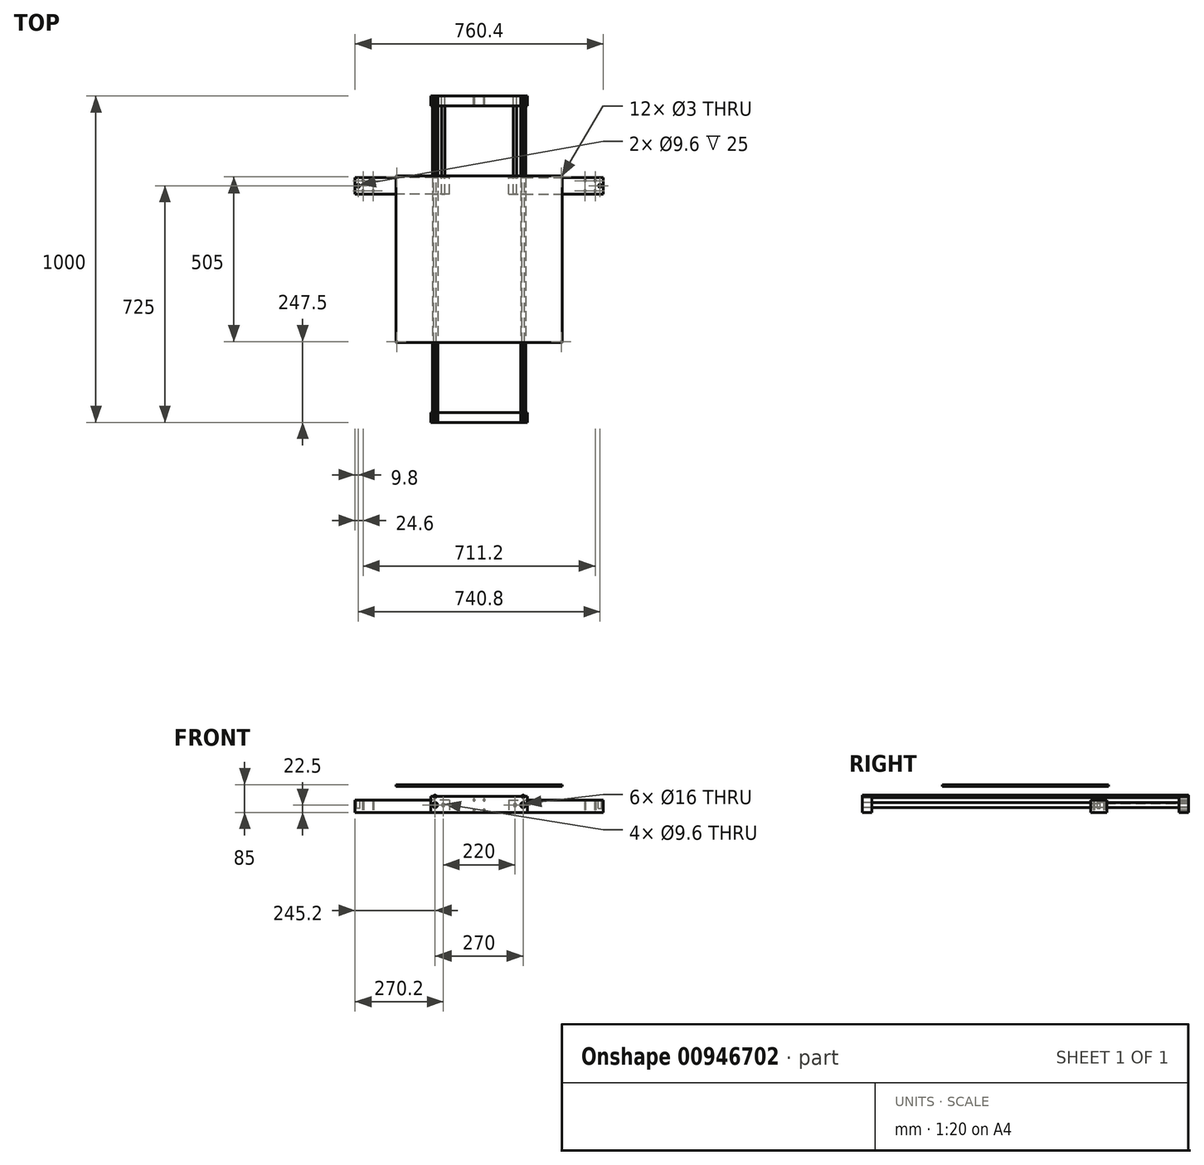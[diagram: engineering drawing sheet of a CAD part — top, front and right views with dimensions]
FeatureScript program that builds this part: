
annotation { "Feature Type Name" : "Feature", "Feature Type Description" : "" }
export const myFeature = defineFeature(function(context is Context, id is Id, definition is map)
    precondition{}
    {
        {
            var Q0;
            Q0=qCreatedBy(makeId("Top.planeOp"),FACE);
            var sketch = newSketch(context, id + "F0", { "sketchPlane" : qUnion([Q0])});
            skLineSegment(sketch, "E0.bottom", {"start": v(255, -255) * mm, "end": v(-255, -255) * mm});
            skLineSegment(sketch, "E0.top", {"start": v(255, 255) * mm, "end": v(-255, 255) * mm});
            skLineSegment(sketch, "E0.left", {"start": v(255, -255) * mm, "end": v(255, 255) * mm});
            skLineSegment(sketch, "E0.right", {"start": v(-255, -255) * mm, "end": v(-255, 255) * mm});
            skPoint(sketch, "E0.middle", {"position": v(0, 0) * mm});
            skLineSegment(sketch, "E1.bottom", {"start": v(-252.5, 252.5) * mm, "end": v(252.5, 252.5) * mm, "construction": true});
            skLineSegment(sketch, "E1.top", {"start": v(-252.5, -252.5) * mm, "end": v(252.5, -252.5) * mm, "construction": true});
            skLineSegment(sketch, "E1.left", {"start": v(-252.5, 252.5) * mm, "end": v(-252.5, -252.5) * mm, "construction": true});
            skLineSegment(sketch, "E1.right", {"start": v(252.5, 252.5) * mm, "end": v(252.5, -252.5) * mm, "construction": true});
            skCircle(sketch, "E2", {"center": v(-252.5, 252.5) * mm, "radius": 1.5 * mm});
            skCircle(sketch, "E3", {"center": v(252.5, 252.5) * mm, "radius": 1.5 * mm});
            skCircle(sketch, "E4", {"center": v(252.5, -252.5) * mm, "radius": 1.5 * mm});
            skCircle(sketch, "E5", {"center": v(-252.5, -252.5) * mm, "radius": 1.5 * mm});
            skSolve(sketch);
        }
        {
            var Q0;
            Q0=makeQuery(id+"F0.imprint","IMPRINT",FACE,{"disambiguationData":[TD([[makeQuery(id+"F0.imprint","IMPRINT",EDGE,{"derivedFrom":sQuery(id+"F0.wireOp",EDGE,"E0.bottom")}),-1.0]])]});
            extrude(context, id + "F1", {"entities" : qUnion([Q0]), "depth" : 5 * mm, "offsetDistance" : 25 * mm});
        }
        {
            var Q0;
            Q0=makeQuery(id+"F1.opExtrude","CAP_FACE",FACE,{"disambiguationData":[OSD([sQuery(id+"F0.wireOp",EDGE,"E0.bottom"),sQuery(id+"F0.wireOp",EDGE,"E0.top"),sQuery(id+"F0.wireOp",EDGE,"E0.left"),sQuery(id+"F0.wireOp",EDGE,"E0.right")])],"isStart":true});
            cPlane(context, id + "F2", {"entities" : qUnion([Q0]), "cplaneType" : CPlaneType.OFFSET, "offset" : 20 * mm, "width" : 150 * mm, "height" : 150 * mm});
        }
        {
            var Q0;
            Q0=qCreatedBy(id+"F2.planeOp",FACE);
            var sketch = newSketch(context, id + "F3", { "sketchPlane" : qUnion([Q0])});
            skCircle(sketch, "E6.0", {"center": v(-252.5, 252.5) * mm, "radius": 1.5 * mm});
            skCircle(sketch, "E6.1", {"center": v(252.5, 252.5) * mm, "radius": 1.5 * mm});
            skCircle(sketch, "E6.2", {"center": v(252.5, -252.5) * mm, "radius": 1.5 * mm});
            skCircle(sketch, "E6.3", {"center": v(-252.5, -252.5) * mm, "radius": 1.5 * mm});
            skLineSegment(sketch, "E7.bottom", {"start": v(135, -135) * mm, "end": v(-135, -135) * mm, "construction": true});
            skLineSegment(sketch, "E7.top", {"start": v(135, 135) * mm, "end": v(-135, 135) * mm, "construction": true});
            skLineSegment(sketch, "E7.left", {"start": v(135, -135) * mm, "end": v(135, 135) * mm, "construction": true});
            skLineSegment(sketch, "E7.right", {"start": v(-135, -135) * mm, "end": v(-135, 135) * mm, "construction": true});
            skPoint(sketch, "E7.middle", {"position": v(0, 0) * mm});
            skCircle(sketch, "E8", {"center": v(-252.5, 252.5) * mm, "radius": 2.5 * mm});
            skCircle(sketch, "E9", {"center": v(252.5, 252.5) * mm, "radius": 2.5 * mm});
            skCircle(sketch, "E10", {"center": v(252.5, -252.5) * mm, "radius": 2.5 * mm});
            skCircle(sketch, "E11", {"center": v(-252.5, -252.5) * mm, "radius": 2.5 * mm});
            skLineSegment(sketch, "E12", {"start": v(-254.27, 250.73) * mm, "end": v(-250.73, 254.27) * mm, "construction": true});
            skLineSegment(sketch, "E13", {"start": v(250.73, 254.27) * mm, "end": v(254.27, 250.73) * mm, "construction": true});
            skLineSegment(sketch, "E14", {"start": v(250.73, -254.27) * mm, "end": v(254.27, -250.73) * mm, "construction": true});
            skLineSegment(sketch, "E15", {"start": v(-254.27, -250.73) * mm, "end": v(-250.73, -254.27) * mm, "construction": true});
            skLineSegment(sketch, "E16", {"start": v(0, -135) * mm, "end": v(-250.73, -254.27) * mm});
            skLineSegment(sketch, "E17", {"start": v(0, -135) * mm, "end": v(250.73, -254.27) * mm});
            skLineSegment(sketch, "E18", {"start": v(-254.27, -250.73) * mm, "end": v(-135, 0) * mm});
            skLineSegment(sketch, "E19", {"start": v(-135, 0) * mm, "end": v(-254.27, 250.73) * mm});
            skLineSegment(sketch, "E20", {"start": v(-250.73, 254.27) * mm, "end": v(0, 135) * mm});
            skLineSegment(sketch, "E21", {"start": v(0, 135) * mm, "end": v(250.73, 254.27) * mm});
            skLineSegment(sketch, "E22", {"start": v(254.27, 250.73) * mm, "end": v(135, 0) * mm});
            skLineSegment(sketch, "E23", {"start": v(135, 0) * mm, "end": v(254.27, -250.73) * mm});
            skLineSegment(sketch, "E24.bottom", {"start": v(-135, 67.5) * mm, "end": v(135, 67.5) * mm, "construction": true});
            skLineSegment(sketch, "E24.top", {"start": v(-135, -67.5) * mm, "end": v(135, -67.5) * mm, "construction": true});
            skLineSegment(sketch, "E24.left", {"start": v(-135, 67.5) * mm, "end": v(-135, -67.5) * mm, "construction": true});
            skLineSegment(sketch, "E24.right", {"start": v(135, 67.5) * mm, "end": v(135, -67.5) * mm, "construction": true});
            skLineSegment(sketch, "E25.bottom", {"start": v(-123, -76.5) * mm, "end": v(-147, -76.5) * mm, "construction": true});
            skLineSegment(sketch, "E25.top", {"start": v(-123, -58.5) * mm, "end": v(-147, -58.5) * mm, "construction": true});
            skLineSegment(sketch, "E25.left", {"start": v(-123, -76.5) * mm, "end": v(-123, -58.5) * mm, "construction": true});
            skLineSegment(sketch, "E25.right", {"start": v(-147, -76.5) * mm, "end": v(-147, -58.5) * mm, "construction": true});
            skPoint(sketch, "E25.middle", {"position": v(-135, -67.5) * mm});
            skLineSegment(sketch, "E26.bottom", {"start": v(123, -76.5) * mm, "end": v(147, -76.5) * mm, "construction": true});
            skLineSegment(sketch, "E26.top", {"start": v(123, -58.5) * mm, "end": v(147, -58.5) * mm, "construction": true});
            skLineSegment(sketch, "E26.left", {"start": v(123, -76.5) * mm, "end": v(123, -58.5) * mm, "construction": true});
            skLineSegment(sketch, "E26.right", {"start": v(147, -76.5) * mm, "end": v(147, -58.5) * mm, "construction": true});
            skPoint(sketch, "E26.middle", {"position": v(135, -67.5) * mm});
            skLineSegment(sketch, "E27.bottom", {"start": v(123, 58.5) * mm, "end": v(147, 58.5) * mm, "construction": true});
            skLineSegment(sketch, "E27.top", {"start": v(123, 76.5) * mm, "end": v(147, 76.5) * mm, "construction": true});
            skLineSegment(sketch, "E27.left", {"start": v(123, 58.5) * mm, "end": v(123, 76.5) * mm, "construction": true});
            skLineSegment(sketch, "E27.right", {"start": v(147, 58.5) * mm, "end": v(147, 76.5) * mm, "construction": true});
            skPoint(sketch, "E27.middle", {"position": v(135, 67.5) * mm});
            skLineSegment(sketch, "E28.bottom", {"start": v(-123, 58.5) * mm, "end": v(-147, 58.5) * mm, "construction": true});
            skLineSegment(sketch, "E28.top", {"start": v(-123, 76.5) * mm, "end": v(-147, 76.5) * mm, "construction": true});
            skLineSegment(sketch, "E28.left", {"start": v(-123, 58.5) * mm, "end": v(-123, 76.5) * mm, "construction": true});
            skLineSegment(sketch, "E28.right", {"start": v(-147, 58.5) * mm, "end": v(-147, 76.5) * mm, "construction": true});
            skPoint(sketch, "E28.middle", {"position": v(-135, 67.5) * mm});
            skCircle(sketch, "E29", {"center": v(-147, -76.5) * mm, "radius": 2.05 * mm});
            skCircle(sketch, "E30", {"center": v(-147, -58.5) * mm, "radius": 2.05 * mm});
            skCircle(sketch, "E31", {"center": v(-123, -58.5) * mm, "radius": 2.05 * mm});
            skCircle(sketch, "E32", {"center": v(-123, -76.5) * mm, "radius": 2.05 * mm});
            skCircle(sketch, "E33", {"center": v(123, -76.5) * mm, "radius": 2.05 * mm});
            skCircle(sketch, "E34", {"center": v(147, -76.5) * mm, "radius": 2.05 * mm});
            skCircle(sketch, "E35", {"center": v(123, -58.5) * mm, "radius": 2.05 * mm});
            skCircle(sketch, "E36", {"center": v(147, -58.5) * mm, "radius": 2.05 * mm});
            skCircle(sketch, "E37", {"center": v(123, 58.5) * mm, "radius": 2.05 * mm});
            skCircle(sketch, "E38", {"center": v(147, 58.5) * mm, "radius": 2.05 * mm});
            skCircle(sketch, "E39", {"center": v(147, 76.5) * mm, "radius": 2.05 * mm});
            skCircle(sketch, "E40", {"center": v(123, 76.5) * mm, "radius": 2.05 * mm});
            skCircle(sketch, "E41", {"center": v(-123, 76.5) * mm, "radius": 2.05 * mm});
            skCircle(sketch, "E42", {"center": v(-147, 76.5) * mm, "radius": 2.05 * mm});
            skCircle(sketch, "E43", {"center": v(-147, 58.5) * mm, "radius": 2.05 * mm});
            skCircle(sketch, "E44", {"center": v(-123, 58.5) * mm, "radius": 2.05 * mm});
            skSolve(sketch);
        }
        {
            var Q0;
            Q0=qCreatedBy(makeId("Front.planeOp"),FACE);
            var sketch = newSketch(context, id + "F4", { "sketchPlane" : qUnion([Q0])});
            skPoint(sketch, "E45.0", {"position": v(-135, -20) * mm});
            skCircle(sketch, "E46", {"center": v(-135, -31) * mm, "radius": 4 * mm});
            skPoint(sketch, "E47.0", {"position": v(135, -20) * mm});
            skCircle(sketch, "E48", {"center": v(135, -31) * mm, "radius": 4 * mm});
            skSolve(sketch);
        }
        {
            var Q0;
            Q0=makeQuery(id+"F4.imprint","IMPRINT",FACE,{"disambiguationData":[TD([[makeQuery(id+"F4.imprint","IMPRINT",EDGE,{"derivedFrom":sQuery(id+"F4.wireOp",EDGE,"E46")}),1.0]])]});
            var Q1;
            Q1=makeQuery(id+"F4.imprint","IMPRINT",FACE,{"disambiguationData":[TD([[makeQuery(id+"F4.imprint","IMPRINT",EDGE,{"derivedFrom":sQuery(id+"F4.wireOp",EDGE,"E48")}),1.0]])]});
            var Q2;
            Q2=sQuery(id+"F4.wireOp",EDGE,"E46");
            var Q3;
            Q3=sQuery(id+"F4.wireOp",EDGE,"E48");
            extrude(context, id + "F5", {"entities" : qUnion([Q0, Q1]), "surfaceEntities" : qUnion([Q2, Q3]), "endBound" : BoundingType.SYMMETRIC, "depth" : 1000 * mm, "offsetDistance" : 25 * mm});
        }
        {
            var Q0;
            Q0=makeQuery(id+"F5.opExtrude","CAP_FACE",FACE,{"disambiguationData":[OSD([sQuery(id+"F4.wireOp",EDGE,"E46")])],"isStart":false});
            var sketch = newSketch(context, id + "F6", { "sketchPlane" : qUnion([Q0])});
            skCircle(sketch, "E49.0", {"center": v(-135, -31) * mm, "radius": 4 * mm});
            skCircle(sketch, "E49.1", {"center": v(135, -31) * mm, "radius": 4 * mm});
            skLineSegment(sketch, "E50.bottom", {"start": v(147.5, -80) * mm, "end": v(-147.5, -80) * mm});
            skLineSegment(sketch, "E50.top", {"start": v(147.5, -31) * mm, "end": v(-147.5, -31) * mm});
            skLineSegment(sketch, "E50.left", {"start": v(147.5, -80) * mm, "end": v(147.5, -31) * mm});
            skLineSegment(sketch, "E50.right", {"start": v(-147.5, -80) * mm, "end": v(-147.5, -31) * mm});
            skPoint(sketch, "E50.middle", {"position": v(0, -55.5) * mm});
            skLineSegment(sketch, "E51", {"start": v(-135, -80) * mm, "end": v(-135, -35) * mm, "construction": true});
            skPoint(sketch, "E52", {"position": v(-135, -57.5) * mm});
            skCircle(sketch, "E53", {"center": v(-135, -57.5) * mm, "radius": 8 * mm});
            skLineSegment(sketch, "E54", {"start": v(135, -80) * mm, "end": v(135, -35) * mm, "construction": true});
            skPoint(sketch, "E55", {"position": v(135, -57.5) * mm});
            skCircle(sketch, "E56", {"center": v(135, -57.5) * mm, "radius": 8 * mm});
            skArc(sketch, "E57", {"start": v(-127, -31) * mm, "mid": v(-135, -28.45) * mm, "end": v(-143, -31) * mm});
            skLineSegment(sketch, "E58", {"start": v(-143, -31) * mm, "end": v(-143, -80) * mm, "construction": true});
            skLineSegment(sketch, "E59", {"start": v(-127, -31) * mm, "end": v(-127, -80) * mm, "construction": true});
            skLineSegment(sketch, "E60", {"start": v(-135, -49.5) * mm, "end": v(-135, -35) * mm, "construction": true});
            skLineSegment(sketch, "E61", {"start": v(135, -49.5) * mm, "end": v(135, -35) * mm, "construction": true});
            skArc(sketch, "E62", {"start": v(143, -31) * mm, "mid": v(135, -28.45) * mm, "end": v(127, -31) * mm});
            skLineSegment(sketch, "E63", {"start": v(127, -31) * mm, "end": v(127, -80) * mm, "construction": true});
            skLineSegment(sketch, "E64", {"start": v(143, -31) * mm, "end": v(143, -80) * mm, "construction": true});
            skSolve(sketch);
        }
        {
            var Q0;
            Q0=makeQuery(id+"F6.imprint","IMPRINT",FACE,{"disambiguationData":[TD([[makeQuery(id+"F6.imprint","IMPRINT",EDGE,{"derivedFrom":sQuery(id+"F6.wireOp",EDGE,"E56")}),1.0]])]});
            var Q1;
            Q1=makeQuery(id+"F6.imprint","IMPRINT",FACE,{"disambiguationData":[TD([[makeQuery(id+"F6.imprint","IMPRINT",EDGE,{"derivedFrom":sQuery(id+"F6.wireOp",EDGE,"E53")}),1.0]])]});
            var Q2;
            Q2=makeQuery(id+"F5.opExtrude","CAP_FACE",FACE,{"disambiguationData":[OSD([sQuery(id+"F4.wireOp",EDGE,"E46")])],"isStart":true});
            extrude(context, id + "F7", {"entities" : qUnion([Q0, Q1]), "endBound" : BoundingType.UP_TO_SURFACE, "oppositeDirection" : true, "depth" : 25 * mm, "endBoundEntityFace" : qUnion([Q2]), "offsetDistance" : 25 * mm});
        }
        {
            var Q0;
            Q0=makeQuery(id+"F6.imprint","IMPRINT",FACE,{"disambiguationData":[TD([[makeQuery(id+"F6.imprint","IMPRINT",EDGE,{"derivedFrom":sQuery(id+"F6.wireOp",EDGE,"E50.bottom")}),-1.0]])]});
            var Q1;
            {var subQ0=sQuery(id+"F6.wireOp",EDGE,"E57");var subQ1=sQuery(id+"F6.wireOp",EDGE,"E49.0");var subQ2=makeQuery(id+"F6.imprint","INTERSECT",VERTEX,{"disambiguationData":[OD(1.0)],"derivedFrom":[subQ1,subQ0]});Q1=makeQuery(id+"F6.imprint","IMPRINT",FACE,{"disambiguationData":[TD([[makeQuery(id+"F6.imprint","IMPRINT",EDGE,{"disambiguationData":[TD([[subQ2,-1.0]])],"derivedFrom":subQ1}),-1.0]])]});}
            var Q2;
            {var subQ0=sQuery(id+"F6.wireOp",EDGE,"E57");var subQ1=sQuery(id+"F6.wireOp",EDGE,"E49.0");var subQ2=makeQuery(id+"F6.imprint","INTERSECT",VERTEX,{"disambiguationData":[OD(0.0)],"derivedFrom":[subQ1,subQ0]});Q2=makeQuery(id+"F6.imprint","IMPRINT",FACE,{"disambiguationData":[TD([[makeQuery(id+"F6.imprint","IMPRINT",EDGE,{"disambiguationData":[TD([[subQ2,1.0]])],"derivedFrom":subQ1}),-1.0]])]});}
            var Q3;
            {var subQ0=sQuery(id+"F6.wireOp",EDGE,"E62");var subQ1=sQuery(id+"F6.wireOp",EDGE,"E49.1");var subQ2=makeQuery(id+"F6.imprint","INTERSECT",VERTEX,{"disambiguationData":[OD(1.0)],"derivedFrom":[subQ1,subQ0]});Q3=makeQuery(id+"F6.imprint","IMPRINT",FACE,{"disambiguationData":[TD([[makeQuery(id+"F6.imprint","IMPRINT",EDGE,{"disambiguationData":[TD([[subQ2,-1.0]])],"derivedFrom":subQ1}),-1.0]])]});}
            var Q4;
            {var subQ0=sQuery(id+"F6.wireOp",EDGE,"E62");var subQ1=sQuery(id+"F6.wireOp",EDGE,"E49.1");var subQ2=makeQuery(id+"F6.imprint","INTERSECT",VERTEX,{"disambiguationData":[OD(0.0)],"derivedFrom":[subQ1,subQ0]});Q4=makeQuery(id+"F6.imprint","IMPRINT",FACE,{"disambiguationData":[TD([[makeQuery(id+"F6.imprint","IMPRINT",EDGE,{"disambiguationData":[TD([[subQ2,1.0]])],"derivedFrom":subQ1}),-1.0]])]});}
            extrude(context, id + "F8", {"entities" : qUnion([Q0, Q1, Q2, Q3, Q4]), "oppositeDirection" : true, "depth" : 30 * mm, "offsetDistance" : 25 * mm});
        }
        {
            var Q0;
            Q0=makeQuery(id+"F5.opExtrude","CAP_FACE",FACE,{"disambiguationData":[OSD([sQuery(id+"F4.wireOp",EDGE,"E46")])],"isStart":true});
            var sketch = newSketch(context, id + "F9", { "sketchPlane" : qUnion([Q0])});
            skArc(sketch, "E65.0.0", {"start": v(-138.38, -28.87) * mm, "mid": v(-135, -35) * mm, "end": v(-131.62, -28.87) * mm});
            skArc(sketch, "E65.0.1", {"start": v(-131.62, -28.87) * mm, "mid": v(-129.2, -29.72) * mm, "end": v(-127, -31) * mm});
            skLineSegment(sketch, "E65.0.2", {"start": v(-127, -31) * mm, "end": v(127, -31) * mm});
            skArc(sketch, "E65.0.3", {"start": v(127, -31) * mm, "mid": v(129.2, -29.72) * mm, "end": v(131.62, -28.87) * mm});
            skArc(sketch, "E65.0.4", {"start": v(131.62, -28.87) * mm, "mid": v(135, -35) * mm, "end": v(138.38, -28.87) * mm});
            skArc(sketch, "E65.0.5", {"start": v(138.38, -28.87) * mm, "mid": v(140.8, -29.72) * mm, "end": v(143, -31) * mm});
            skLineSegment(sketch, "E65.0.6", {"start": v(143, -31) * mm, "end": v(147.5, -31) * mm});
            skLineSegment(sketch, "E65.0.7", {"start": v(147.5, -31) * mm, "end": v(147.5, -80) * mm});
            skLineSegment(sketch, "E65.0.8", {"start": v(147.5, -80) * mm, "end": v(-147.5, -80) * mm});
            skLineSegment(sketch, "E65.0.9", {"start": v(-147.5, -80) * mm, "end": v(-147.5, -31) * mm});
            skLineSegment(sketch, "E65.0.10", {"start": v(-147.5, -31) * mm, "end": v(-143, -31) * mm});
            skArc(sketch, "E65.0.11", {"start": v(-143, -31) * mm, "mid": v(-140.8, -29.72) * mm, "end": v(-138.38, -28.87) * mm});
            skCircle(sketch, "E66.0", {"center": v(-135, -57.5) * mm, "radius": 8 * mm});
            skCircle(sketch, "E66.1", {"center": v(135, -57.5) * mm, "radius": 8 * mm});
            skLineSegment(sketch, "E67", {"start": v(-135, -57.5) * mm, "end": v(135, -57.5) * mm, "construction": true});
            skCircle(sketch, "E68", {"center": v(-110, -57.5) * mm, "radius": 4.8 * mm});
            skCircle(sketch, "E69", {"center": v(110, -57.5) * mm, "radius": 4.8 * mm});
            skLineSegment(sketch, "E70.bottom", {"start": v(15.5, -73) * mm, "end": v(-15.5, -73) * mm, "construction": true});
            skLineSegment(sketch, "E70.top", {"start": v(15.5, -42) * mm, "end": v(-15.5, -42) * mm, "construction": true});
            skLineSegment(sketch, "E70.left", {"start": v(15.5, -73) * mm, "end": v(15.5, -42) * mm, "construction": true});
            skLineSegment(sketch, "E70.right", {"start": v(-15.5, -73) * mm, "end": v(-15.5, -42) * mm, "construction": true});
            skPoint(sketch, "E70.middle", {"position": v(0, -57.5) * mm});
            skSolve(sketch);
        }
        {
            var Q0;
            Q0=makeQuery(id+"F9.imprint","IMPRINT",FACE,{"disambiguationData":[TD([[makeQuery(id+"F9.imprint","IMPRINT",EDGE,{"derivedFrom":sQuery(id+"F9.wireOp",EDGE,"E65.0.0")}),-1.0]])]});
            extrude(context, id + "F10", {"entities" : qUnion([Q0]), "oppositeDirection" : true, "depth" : 30 * mm, "offsetDistance" : 25 * mm});
        }
        {
            var Q0;
            Q0 = qSketchRegion(id + "F12", true);
            var Q1;
            Q1=makeQuery(id+"F9.imprint","IMPRINT",FACE,{"disambiguationData":[TD([[makeQuery(id+"F9.imprint","IMPRINT",EDGE,{"derivedFrom":sQuery(id+"F9.wireOp",EDGE,"E68")}),1.0]])]});
            var Q2;
            Q2=makeQuery(id+"F9.imprint","IMPRINT",FACE,{"disambiguationData":[TD([[makeQuery(id+"F9.imprint","IMPRINT",EDGE,{"derivedFrom":sQuery(id+"F9.wireOp",EDGE,"E69")}),1.0]])]});
            extrude(context, id + "F11", {"entities" : qUnion([Q0, Q1, Q2]), "oppositeDirection" : true, "depth" : 300 * mm, "offsetDistance" : 25 * mm});
        }
        {
            var Q0;
            Q0=makeQuery(id+"F8.opExtrude","SWEPT_FACE",FACE,{"disambiguationData":[OSD([sQuery(id+"F6.wireOp",EDGE,"E50.bottom")])]});
            var sketch = newSketch(context, id + "F12", { "sketchPlane" : qUnion([Q0])});
            skLineSegment(sketch, "E71.0", {"start": v(-105.2, -200) * mm, "end": v(-114.8, -200) * mm, "construction": true});
            skLineSegment(sketch, "E72.bottom", {"start": v(-90.2, -200) * mm, "end": v(-380.2, -200) * mm});
            skLineSegment(sketch, "E72.top", {"start": v(-90.2, -250) * mm, "end": v(-380.2, -250) * mm});
            skLineSegment(sketch, "E72.left", {"start": v(-90.2, -200) * mm, "end": v(-90.2, -250) * mm});
            skLineSegment(sketch, "E72.right", {"start": v(-380.2, -200) * mm, "end": v(-380.2, -250) * mm});
            skSolve(sketch);
        }
        {
            var Q0;
            Q0=makeQuery(id+"F12.imprint","IMPRINT",FACE,{"disambiguationData":[TD([[makeQuery(id+"F12.imprint","IMPRINT",EDGE,{"derivedFrom":sQuery(id+"F12.wireOp",EDGE,"E72.bottom")}),1.0]])]});
            var Q1;
            Q1=sQuery(id+"F9.wireOp",VERTEX,"E65.0.3.center");
            extrude(context, id + "F13", {"entities" : qUnion([Q0]), "endBound" : BoundingType.UP_TO_VERTEX, "oppositeDirection" : true, "depth" : 25 * mm, "endBoundEntityVertex" : qUnion([Q1]), "offsetDistance" : 25 * mm});
        }
        {
            var Q0;
            Q0=makeQuery(id+"F13.opExtrude","CAP_FACE",FACE,{"disambiguationData":[OSD([sQuery(id+"F12.wireOp",EDGE,"E72.bottom"),sQuery(id+"F12.wireOp",EDGE,"E72.top"),sQuery(id+"F12.wireOp",EDGE,"E72.left"),sQuery(id+"F12.wireOp",EDGE,"E72.right")])],"isStart":false});
            var sketch = newSketch(context, id + "F14", { "sketchPlane" : qUnion([Q0])});
            skLineSegment(sketch, "E73.0", {"start": v(-90.2, 250) * mm, "end": v(-380.2, 250) * mm, "construction": true});
            skLineSegment(sketch, "E73.1", {"start": v(-90.2, 200) * mm, "end": v(-380.2, 200) * mm, "construction": true});
            skLineSegment(sketch, "E73.2", {"start": v(-380.2, 200) * mm, "end": v(-380.2, 250) * mm, "construction": true});
            skLineSegment(sketch, "E73.3", {"start": v(-90.2, 200) * mm, "end": v(-90.2, 250) * mm, "construction": true});
            skLineSegment(sketch, "E74", {"start": v(-90.2, 225) * mm, "end": v(-380.2, 225) * mm, "construction": true});
            skLineSegment(sketch, "E75.bottom", {"start": v(-324.6, 240.5) * mm, "end": v(-355.6, 240.5) * mm});
            skLineSegment(sketch, "E75.top", {"start": v(-324.6, 209.5) * mm, "end": v(-355.6, 209.5) * mm});
            skLineSegment(sketch, "E75.left", {"start": v(-324.6, 240.5) * mm, "end": v(-324.6, 209.5) * mm});
            skLineSegment(sketch, "E75.right", {"start": v(-355.6, 240.5) * mm, "end": v(-355.6, 209.5) * mm});
            skPoint(sketch, "E75.middle", {"position": v(-340.1, 225) * mm});
            skCircle(sketch, "E76", {"center": v(-370.4, 225) * mm, "radius": 4.8 * mm});
            skSolve(sketch);
        }
        {
            var Q0;
            Q0=makeQuery(id+"F14.imprint","IMPRINT",FACE,{"disambiguationData":[TD([[makeQuery(id+"F14.imprint","IMPRINT",EDGE,{"derivedFrom":sQuery(id+"F14.wireOp",EDGE,"E76")}),1.0]])]});
            extrude(context, id + "F15", {"entities" : qUnion([Q0]), "operationType" : NewBodyOperationType.REMOVE, "oppositeDirection" : true, "depth" : 25 * mm, "offsetDistance" : 25 * mm});
        }
        {
            var Q0;
            Q0=makeQuery(id+"F13.opExtrude","CAP_FACE",FACE,{"disambiguationData":[OSD([sQuery(id+"F12.wireOp",EDGE,"E72.bottom"),sQuery(id+"F12.wireOp",EDGE,"E72.top"),sQuery(id+"F12.wireOp",EDGE,"E72.left"),sQuery(id+"F12.wireOp",EDGE,"E72.right")])],"isStart":true});
            var sketch = newSketch(context, id + "F16", { "sketchPlane" : qUnion([Q0])});
            skPoint(sketch, "E77.0", {"position": v(-324.6, -209.5) * mm});
            skPoint(sketch, "E77.1", {"position": v(-324.6, -240.5) * mm});
            skPoint(sketch, "E77.2", {"position": v(-355.6, -240.5) * mm});
            skPoint(sketch, "E77.3", {"position": v(-355.6, -209.5) * mm});
            skSolve(sketch);
        }
        {
            var Q0;
            Q0=makeQuery(id+"F11.opExtrude","SWEPT_BODY",BODY,{"disambiguationData":[OSD([sQuery(id+"F9.wireOp",EDGE,"E69")])]});
            var Q1;
            Q1=makeQuery(id+"F7.opExtrude","SWEPT_BODY",BODY,{"disambiguationData":[OSD([sQuery(id+"F6.wireOp",EDGE,"E53")])]});
            var Q2;
            Q2=makeQuery(id+"F13.opExtrude","SWEPT_BODY",BODY,{"disambiguationData":[OSD([sQuery(id+"F12.wireOp",EDGE,"E72.bottom"),sQuery(id+"F12.wireOp",EDGE,"E72.top"),sQuery(id+"F12.wireOp",EDGE,"E72.left"),sQuery(id+"F12.wireOp",EDGE,"E72.right")])]});
            booleanBodies(context, id + "F17", {"operationType" : BooleanOperationType.SUBTRACTION, "tools" : qUnion([Q0, Q1]), "targets" : qUnion([Q2]), "keepTools" : true});
        }
        {
            var Q0;
            Q0=sQuery(id+"F16.wireOp",VERTEX,"E77.1");
            var Q1;
            Q1=sQuery(id+"F16.wireOp",VERTEX,"E77.2");
            var Q2;
            Q2=sQuery(id+"F16.wireOp",VERTEX,"E77.3");
            var Q3;
            Q3=sQuery(id+"F16.wireOp",VERTEX,"E77.0");
            var Q4;
            Q4=makeQuery(id+"F13.opExtrude","SWEPT_BODY",BODY,{"disambiguationData":[OSD([sQuery(id+"F12.wireOp",EDGE,"E72.bottom"),sQuery(id+"F12.wireOp",EDGE,"E72.top"),sQuery(id+"F12.wireOp",EDGE,"E72.left"),sQuery(id+"F12.wireOp",EDGE,"E72.right")])]});
            hole(context, id + "F18", {"style" : HoleStyle.C_SINK, "endStyle" : HoleEndStyle.THROUGH, "holeDiameter" : 3 * mm, "cSinkDiameter" : 6 * mm, "cSinkAngle" : 90 * degree, "majorDiameter" : 5 * mm, "isTappedThrough" : true, "tappedDepth" : 12 * mm, "tapClearance" : 3, "startFromSketch" : true, "locations" : qUnion([Q0, Q1, Q2, Q3]), "scope" : qUnion([Q4])});
        }
        {
            var Q0;
            Q0=sQuery(id+"F9.wireOp",VERTEX,"E70.top.end");
            var Q1;
            Q1=sQuery(id+"F9.wireOp",VERTEX,"E70.top.start");
            var Q2;
            Q2=sQuery(id+"F9.wireOp",VERTEX,"E70.bottom.start");
            var Q3;
            Q3=sQuery(id+"F9.wireOp",VERTEX,"E70.bottom.end");
            var Q4;
            Q4=makeQuery(id+"F10.opExtrude","SWEPT_BODY",BODY,{"disambiguationData":[OSD([sQuery(id+"F9.wireOp",EDGE,"E65.0.0"),sQuery(id+"F9.wireOp",EDGE,"E65.0.1"),sQuery(id+"F9.wireOp",EDGE,"E65.0.2"),sQuery(id+"F9.wireOp",EDGE,"E65.0.3"),sQuery(id+"F9.wireOp",EDGE,"E65.0.4"),sQuery(id+"F9.wireOp",EDGE,"E65.0.5"),sQuery(id+"F9.wireOp",EDGE,"E65.0.6"),sQuery(id+"F9.wireOp",EDGE,"E65.0.7"),sQuery(id+"F9.wireOp",EDGE,"E65.0.8"),sQuery(id+"F9.wireOp",EDGE,"E65.0.9"),sQuery(id+"F9.wireOp",EDGE,"E65.0.10"),sQuery(id+"F9.wireOp",EDGE,"E65.0.11"),sQuery(id+"F9.wireOp",EDGE,"E66.0"),sQuery(id+"F9.wireOp",EDGE,"E66.1"),sQuery(id+"F9.wireOp",EDGE,"E68"),sQuery(id+"F9.wireOp",EDGE,"E69")])]});
            hole(context, id + "F19", {"style" : HoleStyle.C_SINK, "endStyle" : HoleEndStyle.THROUGH, "holeDiameter" : 3 * mm, "cSinkDiameter" : 6 * mm, "cSinkAngle" : 90 * degree, "majorDiameter" : 5 * mm, "isTappedThrough" : true, "tappedDepth" : 12 * mm, "tapClearance" : 3, "startFromSketch" : true, "locations" : qUnion([Q0, Q1, Q2, Q3]), "scope" : qUnion([Q4])});
        }
        {
            var Q0;
            Q0=makeQuery(id+"F13.opExtrude","SWEPT_BODY",BODY,{"disambiguationData":[OSD([sQuery(id+"F12.wireOp",EDGE,"E72.bottom"),sQuery(id+"F12.wireOp",EDGE,"E72.top"),sQuery(id+"F12.wireOp",EDGE,"E72.left"),sQuery(id+"F12.wireOp",EDGE,"E72.right")])]});
            var Q1;
            Q1=qCreatedBy(makeId("Right.planeOp"),FACE);
            mirror(context, id + "F20", {"entities" : qUnion([Q0]), "mirrorPlane" : qUnion([Q1])});
        }
    });
